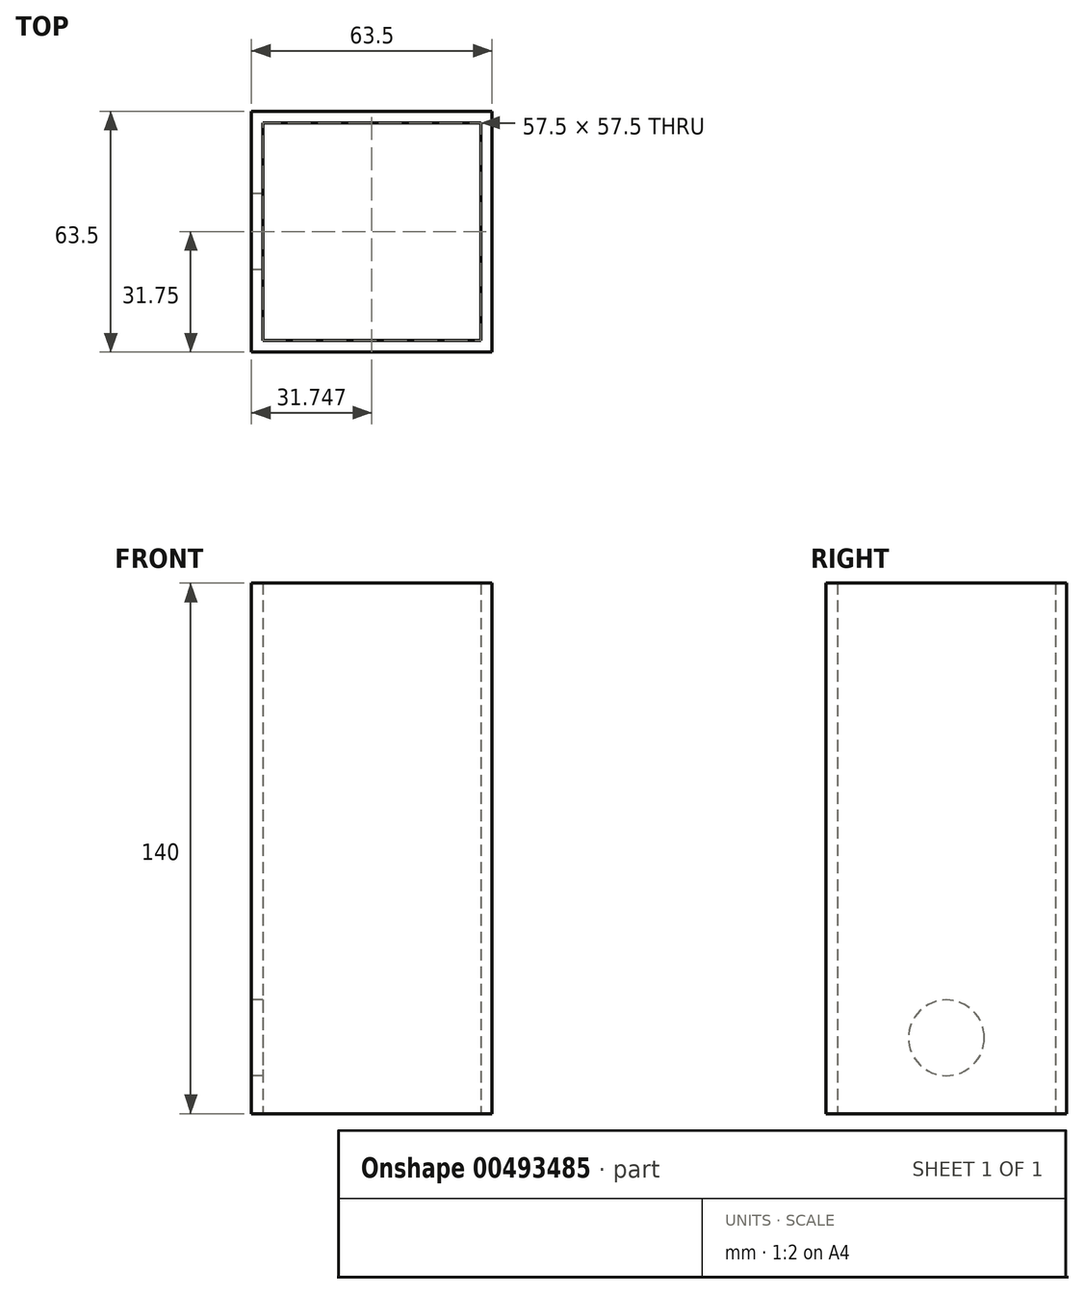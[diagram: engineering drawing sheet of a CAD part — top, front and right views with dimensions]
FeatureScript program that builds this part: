
annotation { "Feature Type Name" : "Feature", "Feature Type Description" : "" }
export const myFeature = defineFeature(function(context is Context, id is Id, definition is map)
    precondition{}
    {
        {
            var Q0;
            Q0=qCreatedBy(makeId("Top.planeOp"),FACE);
            var sketch = newSketch(context, id + "F0", { "sketchPlane" : qUnion([Q0])});
            skLineSegment(sketch, "E0.bottom", {"start": v(-26.31, 30.47) * mm, "end": v(31.19, 30.47) * mm});
            skLineSegment(sketch, "E0.top", {"start": v(-26.31, -27.03) * mm, "end": v(31.19, -27.03) * mm});
            skLineSegment(sketch, "E0.left", {"start": v(-26.31, 30.47) * mm, "end": v(-26.31, -27.03) * mm});
            skLineSegment(sketch, "E0.right", {"start": v(31.19, 30.47) * mm, "end": v(31.19, -27.03) * mm});
            skLineSegment(sketch, "E1.bottom", {"start": v(-29.31, 33.47) * mm, "end": v(34.19, 33.47) * mm});
            skLineSegment(sketch, "E1.top", {"start": v(-29.31, -30.03) * mm, "end": v(34.19, -30.03) * mm});
            skLineSegment(sketch, "E1.left", {"start": v(-29.31, 33.47) * mm, "end": v(-29.31, -30.03) * mm});
            skLineSegment(sketch, "E1.right", {"start": v(34.19, 33.47) * mm, "end": v(34.19, -30.03) * mm});
            skSolve(sketch);
        }
        {
            var Q0;
            Q0=qSketchRegion(id+"F0",true);
            var Q1;
            Q1 = qSketchRegion(id + "FaACt5fpPCwFAds_1", true);
            extrude(context, id + "F1", {"entities" : qUnion([Q0, Q1]), "offsetDistance" : 25 * mm, "depth" : 140 * mm});
        }
        {
            var Q0;
            Q0=makeQuery(id+"F1.opExtrude","SWEPT_FACE",FACE,{"disambiguationData":[OSD([sQuery(id+"F0.wireOp",EDGE,"E1.left")])]});
            var sketch = newSketch(context, id + "F2", { "sketchPlane" : qUnion([Q0])});
            skCircle(sketch, "E2", {"center": v(-1.72, 20) * mm, "radius": 10 * mm});
            skSolve(sketch);
        }
        {
            var Q0;
            Q0 = qSketchRegion(id + "F2", true);
            extrude(context, id + "F3", {"entities" : qUnion([Q0]), "operationType" : NewBodyOperationType.REMOVE, "oppositeDirection" : true, "depth" : 3 * mm, "offsetDistance" : 25 * mm});
        }
    });
